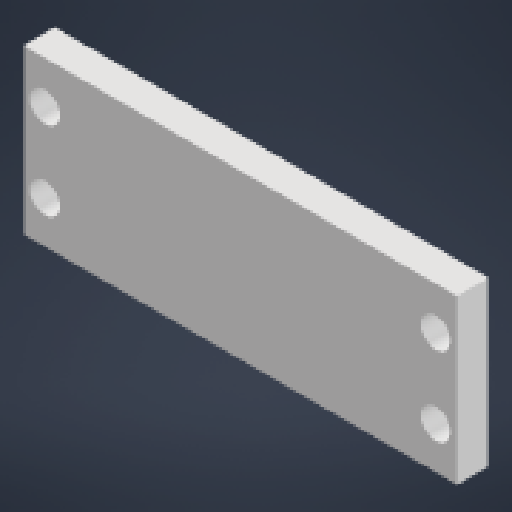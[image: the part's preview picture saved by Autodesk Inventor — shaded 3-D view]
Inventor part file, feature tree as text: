
AUTODESK INVENTOR PART (.ipt)
format: ipt  version: 2024.2 (Build 282272000, 272)  size: 174,592 bytes
history: native  units: in
note: dims shown in document units (in); Inventor stores cm internally (conversion verified against a paired STEP export)
features: extrude x3, sketch x3, other x3, projected_geometry x2, plane x1, reference x1
ambient origin geometry x8: Origin, YZ Plane, XZ Plane, XY Plane, X Axis, Y Axis, Z Axis, Center Point
bodies: Solid1 (feature_tree)
feature tree (13):
  extrude  "Extrusion1"  TaperAngle=0.0deg  [1 undecoded]
  plane  "Work Plane1"
  extrude  "Extrusion3"  TaperAngle=0.0deg  [1 undecoded]
  extrude  "Extrusion4"  Depth=0.2362in
  sketch  "Sketch1"  dims[d0=0.0in d1=0.0in]
  sketch  "Sketch3"  dims[d2=0.0098in d3=0.0in]
  reference  "Reference3"
  sketch  "Sketch4"  dims[d4=0.0in d5=0.0098in d6=0.0098in d7=0.1496in d8=0.1496in d9=0.1496in d10=0.1496in d11=0.2756in d12=0.0in d16=0.0in d17=1.0in d18=0.0in d19=0.0787in d20=0.1496in d21=0.743in d23=0.5in d24=0.2362in d25=0.0in]
  other  "<userpath>\Desktop\Robotics\Cad\Powerplay_Fun\Parts\Claw_Assembly.iam"
  other  "Claw_Assembly.iam"
  other  "Bottom_Claw_Mount:1"
  projected_geometry  "Project Cut Edges1"
  projected_geometry  "Project Cut Edges2"
note: 2 required parameter values undecoded (feature->parameter linkage not recoverable at this tier; creation-order binding heuristic only, values carry confidence <= 0.55)
